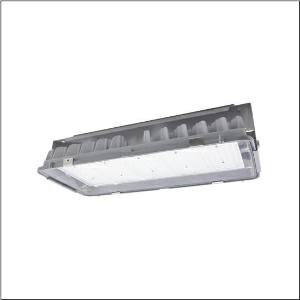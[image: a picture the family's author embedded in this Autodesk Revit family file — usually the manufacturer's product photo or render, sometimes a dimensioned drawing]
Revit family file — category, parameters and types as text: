
# Revit family: highbay_11xtreme_51hf62da4hma
name_source: partatom
category: Lighting Fixtures
units: mm (PartAtom-declared; Revit-internal decimal feet)

## family parameters
Cut with Voids When Loaded = No
Host = Face
Light Source = No
Part Type = Normal
Room Calculation Point = No
Round Connector Dimension = Use Diameter
Shared = No

## types (1)
- --- (1 x LED, 18500 lm, 96.5 W, 4000K)
    Apparent Load = 97 VA
    CIE Flux Codes = 84 96 100 100 100
    Color Rendering = 80
    Color Temperature = 4000K
    Default Elevation = 1800 mm
    Description = Highbay 11Xtreme, LED high bay luminaire, primary light control with lens, of PMMA, primary optical cover: cover, of toughened safety glass, light emission: direct distribution, primary light characteristic: symmetric, installation type: suspended mounting, surface-mounted, 1x LED module,for 1x LED, rated luminous flux: 18.500lm, luminous efficacy: 192lm/W, light colour: 840, colour temperature: 4000K, with cable H07RN-F 5x 1.5mm², mains connection: 220..240V, AC, 50/60Hz, cable length: 1,5m, rated input power: 97W, luminaire housing, of diecast aluminium, coated, silver, length: 595mm, width: 280mm, height: 195mm, protection rating (complete): IP66, insulation class (complete): insulation class I (protective earthing), certification: CE, ENEC, UKCA, protection symbol: D, ball protection: ball impact resistant according to DIN VDE 0710 part 13 (with chain suspension), impact resistance: IK08, permissible operating ambient temperature: -25..+70°C, reducing of maximum allowable ambient temperature of 5°C with ceiling mounting, packaging unit: 1 piece
    Height = 157 mm
    Lamp = 1 x LED
    Lamp Light Flux = 18500 lm
    Lamp Power = 96.5 W
    Lamp count = 1
    Length = 593 mm
    Luminous efficacy = 192 lm/W
    Manufacturer = Siteco
    ModVariant = No
    Model = 51HF62DA4HMA
    Mounting Place = Ceiling
    Mounting Type = Pendant
    Number of Poles = 1
    OnlyDefault = Yes
    Power Factor = 1
    Product Name = Highbay 11Xtreme
    Product group = LED high bay luminaire
    ProductGroupID = 903
    Protection Class = Protection class I
    Protection Degree = IP 66
    RLX_Detail_Level = 1
    RLX_Emergency_Light_Flux = 0 lm
    RLX_Emergency_Type = 0
    RLX_Emergency_Type_DB = No
    RlxData = <blob elided: 28257 chars, md5=cd62ccf7>
    Socket = socket
    Standby Power = 0 W
    System Light Flux = 18500 lm
    System Power = 97 W
    Type Comments = factory setting: luminous flux: 100 % | dim-lin: 254 | 652 mA
    Type Image = l_1258342.jpg
    URL = http://relux.com
    VarID = @adj_052683
    Voltage = 0 V
    Weight = 0.00 kg
    Width = 568 mm

## geometry (parser evidence)
native form markers: Blend x4, Sweep x10
no freeform markers — native parametric forms only
